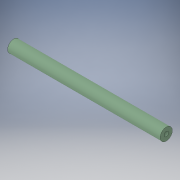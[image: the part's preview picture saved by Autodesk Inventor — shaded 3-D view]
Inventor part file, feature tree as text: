
AUTODESK INVENTOR PART (.ipt)
format: ipt  version: 2019 (Build 230136000, 136)  size: 102,912 bytes
history: native  units: mm
features: extrude x2, sketch x2
ambient origin geometry x8: Origin, YZ Plane, XZ Plane, XY Plane, X Axis, Y Axis, Z Axis, Center Point
bodies: Solid1 (feature_tree)
feature tree (4):
  extrude  "Extrusion1"  Depth=200.0mm TaperAngle=0.0deg
  extrude  "Extrusion2"  Depth=200.0mm TaperAngle=0.0deg
  sketch  "Sketch1"  dims[d0=16.0mm d1=200.0mm d2=0.0mm]
  sketch  "Sketch2"  dims[d3=6.0mm d4=200.0mm d5=0.0mm]
